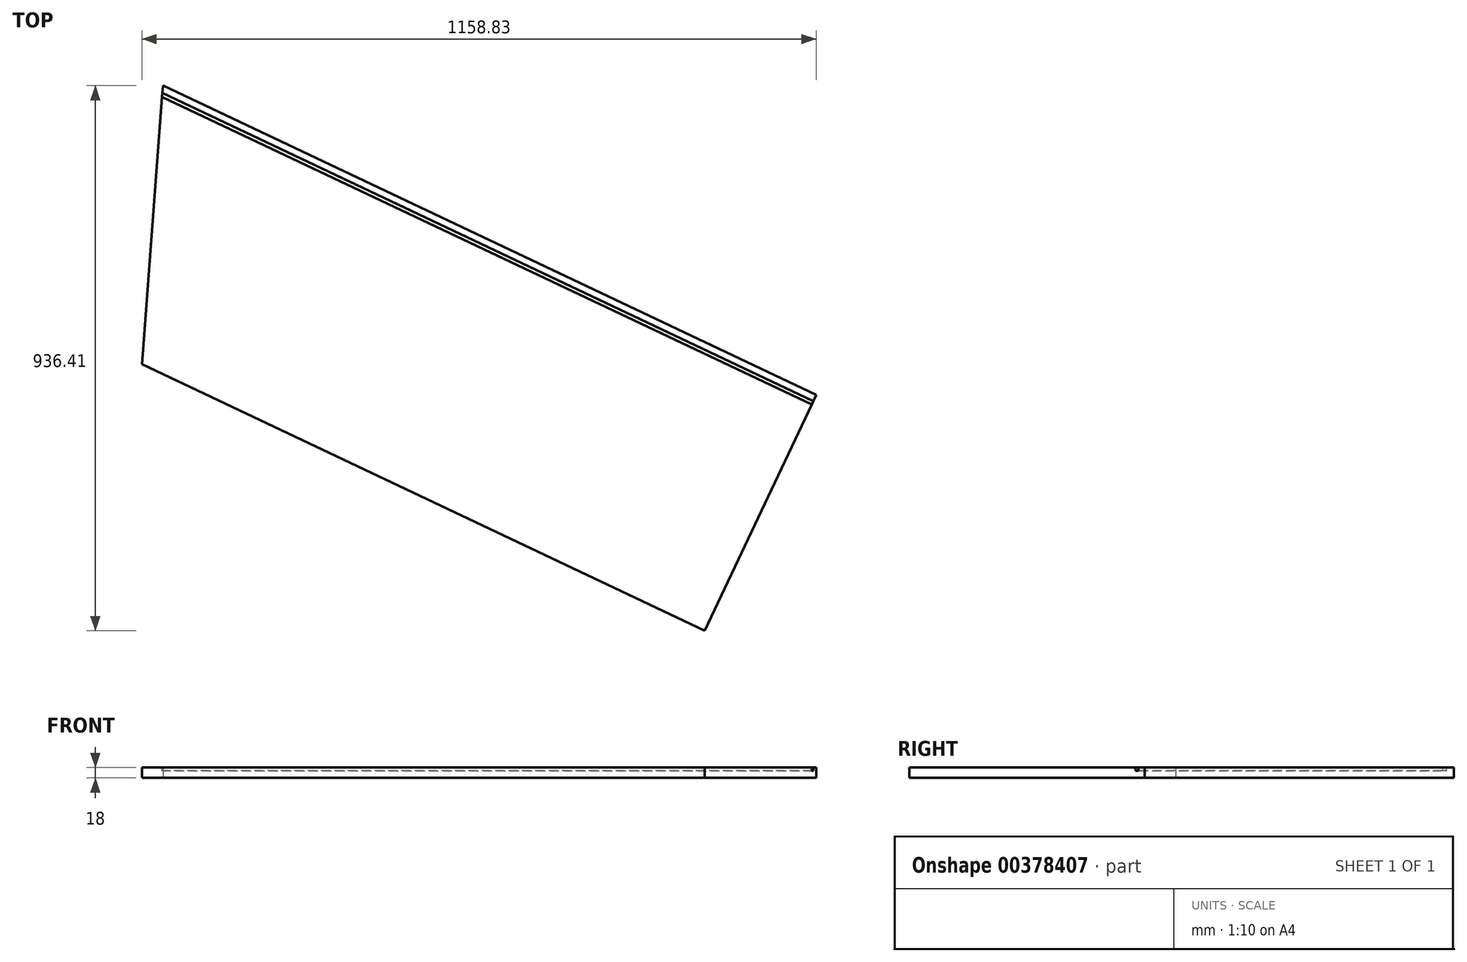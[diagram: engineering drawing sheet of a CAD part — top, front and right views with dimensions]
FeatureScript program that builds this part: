
annotation { "Feature Type Name" : "Feature", "Feature Type Description" : "" }
export const myFeature = defineFeature(function(context is Context, id is Id, definition is map)
    precondition{}
    {
        {
            var Q0;
            Q0=qCreatedBy(makeId("Top.planeOp"),FACE);
            var sketch = newSketch(context, id + "F0", { "sketchPlane" : qUnion([Q0])});
            skLineSegment(sketch, "E0", {"start": v(-205.56, 331.82) * mm, "end": v(917.03, -199.56) * mm});
            skLineSegment(sketch, "E1", {"start": v(917.03, -199.56) * mm, "end": v(725.3, -604.59) * mm});
            skLineSegment(sketch, "E2", {"start": v(725.3, -604.59) * mm, "end": v(-241.8, -146.81) * mm});
            skLineSegment(sketch, "E3", {"start": v(-205.56, 331.82) * mm, "end": v(-241.8, -146.81) * mm});
            skSolve(sketch);
        }
        {
            var Q0;
            Q0 = qSketchRegion(id + "F0", true);
            extrude(context, id + "F1", {"entities" : qUnion([Q0]), "depth" : 18 * mm});
        }
        {
            var Q0;
            Q0=makeQuery(id+"F1.opExtrude","CAP_FACE",FACE,{"disambiguationData":[OSD([sQuery(id+"F0.wireOp",EDGE,"hm7g1ifC-j8bG-lpUX-5ii8-XuTQjQwk62bA"),sQuery(id+"F0.wireOp",EDGE,"E0"),sQuery(id+"F0.wireOp",EDGE,"E1"),sQuery(id+"F0.wireOp",EDGE,"E2")])],"isStart":false});
            var sketch = newSketch(context, id + "F2", { "sketchPlane" : qUnion([Q0])});
            skLineSegment(sketch, "E4", {"start": v(911.9, -210.4) * mm, "end": v(-206.53, 319) * mm});
            skLineSegment(sketch, "E5", {"start": v(-206.53, 319) * mm, "end": v(-207.02, 312.6) * mm});
            skLineSegment(sketch, "E6", {"start": v(-207.02, 312.6) * mm, "end": v(909.33, -215.82) * mm});
            skLineSegment(sketch, "E7", {"start": v(909.33, -215.82) * mm, "end": v(911.9, -210.4) * mm});
            skSolve(sketch);
        }
        {
            var Q0;
            Q0 = qSketchRegion(id + "F2", true);
            extrude(context, id + "F3", {"entities" : qUnion([Q0]), "operationType" : NewBodyOperationType.REMOVE, "oppositeDirection" : true, "depth" : 6 * mm});
        }
    });
